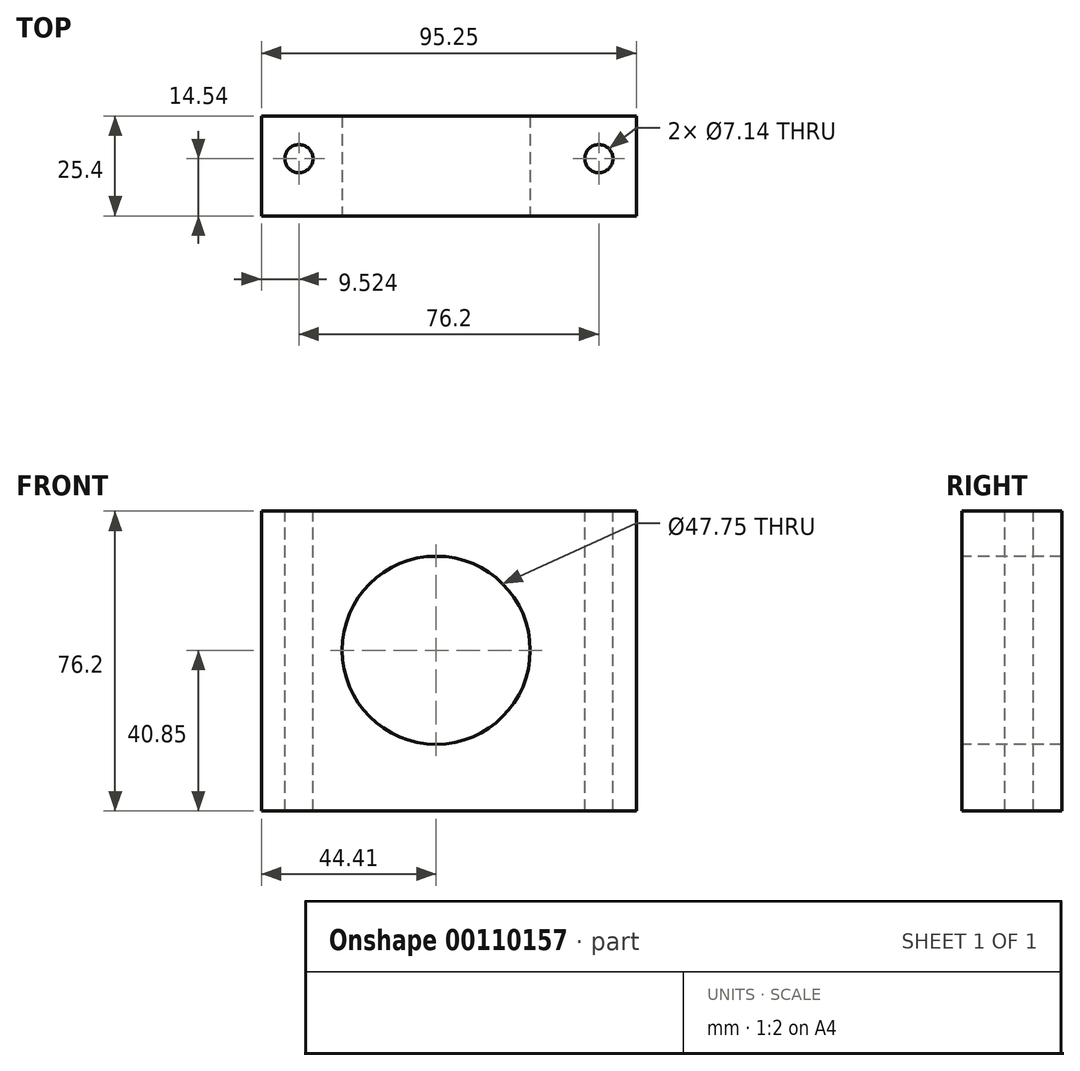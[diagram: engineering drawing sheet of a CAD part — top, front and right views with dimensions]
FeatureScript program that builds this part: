
annotation { "Feature Type Name" : "Feature", "Feature Type Description" : "" }
export const myFeature = defineFeature(function(context is Context, id is Id, definition is map)
    precondition{}
    {
        {
            var Q0;
            Q0=qCreatedBy(makeId("Front.planeOp"),FACE);
            var sketch = newSketch(context, id + "F0", { "sketchPlane" : qUnion([Q0])});
            skLineSegment(sketch, "E0.bottom", {"start": v(-44.41, 35.35) * mm, "end": v(50.84, 35.35) * mm});
            skLineSegment(sketch, "E0.top", {"start": v(-44.41, -40.85) * mm, "end": v(50.84, -40.85) * mm});
            skLineSegment(sketch, "E0.left", {"start": v(-44.41, 35.35) * mm, "end": v(-44.41, -40.85) * mm});
            skLineSegment(sketch, "E0.right", {"start": v(50.84, 35.35) * mm, "end": v(50.84, -40.85) * mm});
            skSolve(sketch);
        }
        {
            var Q0;
            Q0=makeQuery(id+"F0.imprint","IMPRINT",FACE,{"disambiguationData":[TD([[makeQuery(id+"F0.imprint","IMPRINT",EDGE,{"derivedFrom":sQuery(id+"F0.wireOp",EDGE,"E0.bottom")}),-1.0]])]});
            extrude(context, id + "F1", {"entities" : qUnion([Q0]), "depth" : 25.4 * mm});
        }
        {
            var Q0;
            Q0=makeQuery(id+"F1.opExtrude","CAP_FACE",FACE,{"disambiguationData":[OSD([sQuery(id+"F0.wireOp",EDGE,"E0.bottom"),sQuery(id+"F0.wireOp",EDGE,"E0.top"),sQuery(id+"F0.wireOp",EDGE,"E0.left"),sQuery(id+"F0.wireOp",EDGE,"E0.right")])],"isStart":false});
            var sketch = newSketch(context, id + "F2", { "sketchPlane" : qUnion([Q0])});
            skCircle(sketch, "E1", {"center": v(0, 0) * mm, "radius": 23.75 * mm});
            skSolve(sketch);
        }
        {
            var Q0;
            Q0=sQuery(id+"F2.wireOp",VERTEX,"E1.center");
            var Q1;
            Q1=makeQuery(id+"F1.opExtrude","SWEPT_BODY",BODY,{"disambiguationData":[OSD([sQuery(id+"F0.wireOp",EDGE,"E0.bottom"),sQuery(id+"F0.wireOp",EDGE,"E0.top"),sQuery(id+"F0.wireOp",EDGE,"E0.left"),sQuery(id+"F0.wireOp",EDGE,"E0.right")])]});
            hole(context, id + "F3", {"style" : HoleStyle.SIMPLE, "endStyle" : HoleEndStyle.THROUGH, "holeDiameter" : 47.75 * mm, "locations" : qUnion([Q0]), "scope" : qUnion([Q1]), "isTappedThrough" : true});
        }
        {
            var Q0;
            Q0=makeQuery(id+"F1.opExtrude","SWEPT_FACE",FACE,{"disambiguationData":[OSD([sQuery(id+"F0.wireOp",EDGE,"E0.bottom")])]});
            var sketch = newSketch(context, id + "F4", { "sketchPlane" : qUnion([Q0])});
            skCircle(sketch, "E2", {"center": v(41.31, -10.86) * mm, "radius": 3.57 * mm});
            skLineSegment(sketch, "E3", {"start": v(3.21, 0) * mm, "end": v(3.21, -25.4) * mm});
            skCircle(sketch, "E4.MirrorC", {"center": v(-34.89, -10.86) * mm, "radius": 3.57 * mm});
            skSolve(sketch);
        }
        {
            var Q0;
            Q0=sQuery(id+"F4.wireOp",VERTEX,"E4.MirrorC.center");
            var Q1;
            Q1=sQuery(id+"F4.wireOp",VERTEX,"E2.center");
            var Q2;
            Q2=makeQuery(id+"F1.opExtrude","SWEPT_BODY",BODY,{"disambiguationData":[OSD([sQuery(id+"F0.wireOp",EDGE,"E0.bottom"),sQuery(id+"F0.wireOp",EDGE,"E0.top"),sQuery(id+"F0.wireOp",EDGE,"E0.left"),sQuery(id+"F0.wireOp",EDGE,"E0.right")])]});
            hole(context, id + "F5", {"style" : HoleStyle.SIMPLE, "endStyle" : HoleEndStyle.THROUGH, "holeDiameter" : 7.14 * mm, "locations" : qUnion([Q0, Q1]), "scope" : qUnion([Q2]), "isTappedThrough" : true});
        }
    });
